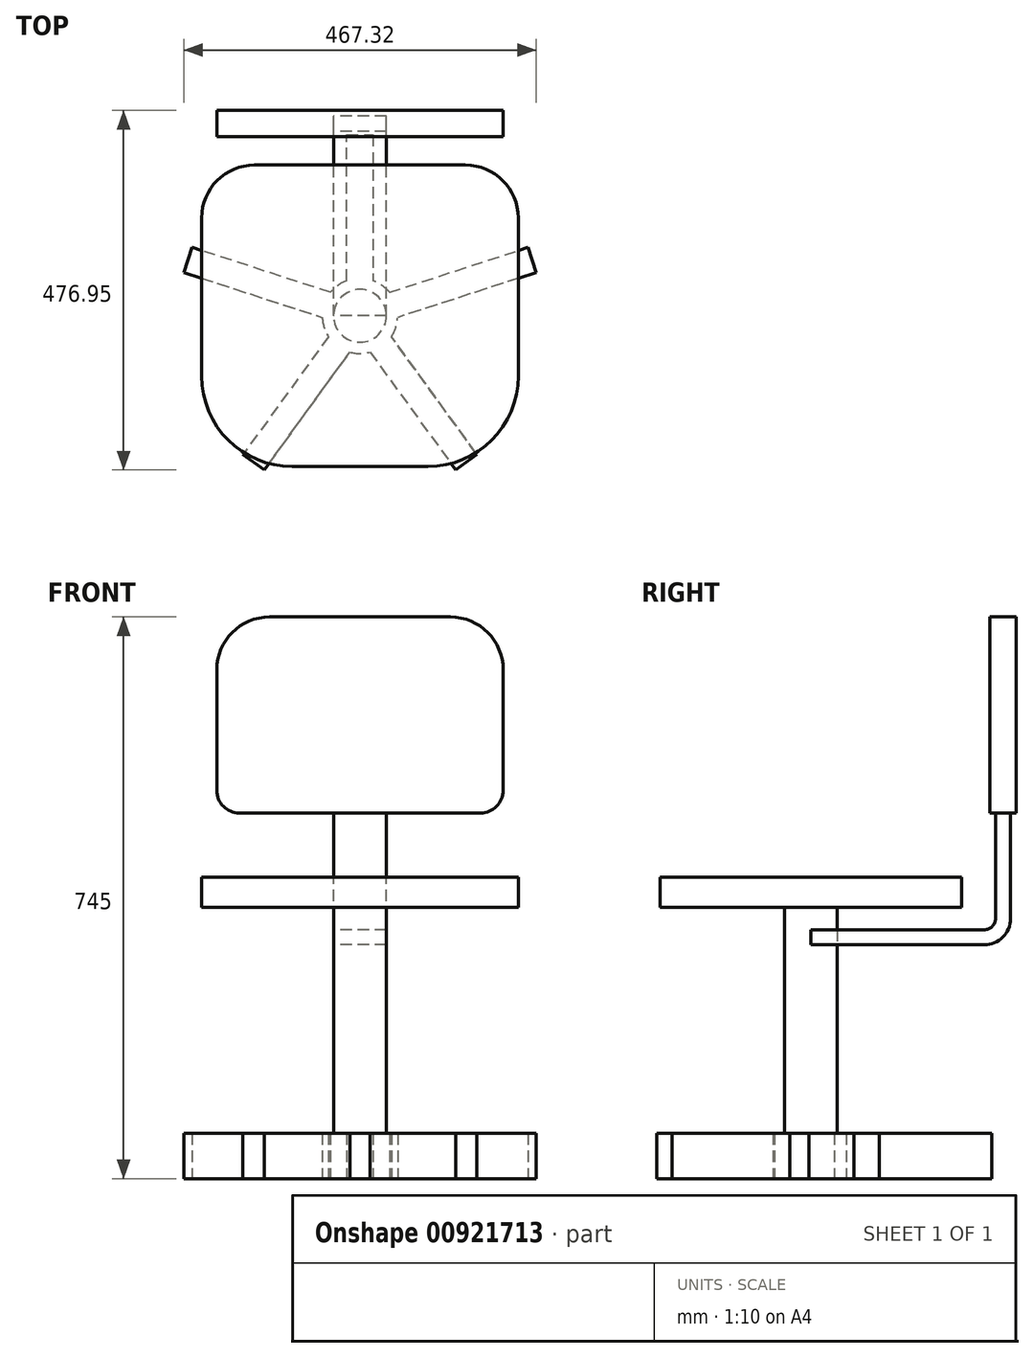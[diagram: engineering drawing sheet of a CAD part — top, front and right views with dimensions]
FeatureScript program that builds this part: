
annotation { "Feature Type Name" : "Feature", "Feature Type Description" : "" }
export const myFeature = defineFeature(function(context is Context, id is Id, definition is map)
    precondition{}
    {
        {
            var Q0;
            Q0=qCreatedBy(makeId("Top.planeOp"),FACE);
            var sketch = newSketch(context, id + "F0", { "sketchPlane" : qUnion([Q0])});
            skCircle(sketch, "E0", {"center": v(0, 0) * mm, "radius": 250 * mm, "construction": true});
            skLineSegment(sketch, "E1", {"start": v(0, 0) * mm, "end": v(0, 276.39) * mm, "construction": true});
            skLineSegment(sketch, "E2", {"start": v(0, 0) * mm, "end": v(-284.26, 92.36) * mm, "construction": true});
            skLineSegment(sketch, "E3", {"start": v(0, 0) * mm, "end": v(-174.03, -239.54) * mm, "construction": true});
            skLineSegment(sketch, "E4", {"start": v(0, 0) * mm, "end": v(174.47, -240.13) * mm, "construction": true});
            skLineSegment(sketch, "E5", {"start": v(0, 0) * mm, "end": v(285.55, 92.78) * mm, "construction": true});
            skArc(sketch, "E6", {"start": v(-49.95, -2.17) * mm, "mid": v(-47.55, -15.45) * mm, "end": v(-41.69, -27.6) * mm});
            skLineSegment(sketch, "E7", {"start": v(-39.14, 31.12) * mm, "end": v(-222.85, 90.8) * mm});
            skLineSegment(sketch, "E8", {"start": v(-222.85, 90.8) * mm, "end": v(-233.66, 57.52) * mm});
            skLineSegment(sketch, "E9", {"start": v(-233.66, 57.52) * mm, "end": v(-49.95, -2.17) * mm});
            skLineSegment(sketch, "E10", {"start": v(-41.69, -27.6) * mm, "end": v(-155.23, -183.88) * mm});
            skLineSegment(sketch, "E11", {"start": v(-155.23, -183.88) * mm, "end": v(-126.91, -204.45) * mm});
            skLineSegment(sketch, "E12", {"start": v(-126.91, -204.45) * mm, "end": v(-13.37, -48.18) * mm});
            skLineSegment(sketch, "E13", {"start": v(13.37, -48.18) * mm, "end": v(126.91, -204.45) * mm});
            skLineSegment(sketch, "E14", {"start": v(126.91, -204.45) * mm, "end": v(155.23, -183.88) * mm});
            skLineSegment(sketch, "E15", {"start": v(155.23, -183.88) * mm, "end": v(41.69, -27.6) * mm});
            skLineSegment(sketch, "E16", {"start": v(39.14, 31.12) * mm, "end": v(222.85, 90.8) * mm});
            skLineSegment(sketch, "E17", {"start": v(222.85, 90.8) * mm, "end": v(233.66, 57.52) * mm});
            skLineSegment(sketch, "E18", {"start": v(233.66, 57.52) * mm, "end": v(49.95, -2.17) * mm});
            skLineSegment(sketch, "E19", {"start": v(-17.5, 46.84) * mm, "end": v(-17.5, 240) * mm});
            skLineSegment(sketch, "E20", {"start": v(-17.5, 240) * mm, "end": v(17.5, 240) * mm});
            skLineSegment(sketch, "E21", {"start": v(17.5, 240) * mm, "end": v(17.5, 46.84) * mm});
            skArc(sketch, "E22.trimOffspring", {"start": v(-13.37, -48.18) * mm, "mid": v(0, -50) * mm, "end": v(13.37, -48.18) * mm});
            skArc(sketch, "E23.trimOffspring", {"start": v(41.69, -27.6) * mm, "mid": v(47.55, -15.45) * mm, "end": v(49.95, -2.17) * mm});
            skArc(sketch, "E24.trimOffspring", {"start": v(39.14, 31.12) * mm, "mid": v(29.39, 40.45) * mm, "end": v(17.5, 46.84) * mm});
            skArc(sketch, "E25.trimOffspring", {"start": v(-17.5, 46.84) * mm, "mid": v(-29.39, 40.45) * mm, "end": v(-39.14, 31.12) * mm});
            skSolve(sketch);
        }
        {
            var Q0;
            Q0 = qSketchRegion(id + "F0", true);
            extrude(context, id + "F1", {"entities" : qUnion([Q0]), "depth" : 60 * mm, "offsetDistance" : 25 * mm});
        }
        {
            var Q0;
            Q0=makeQuery(id+"F1.opExtrude","CAP_FACE",FACE,{"disambiguationData":[OSD([sQuery(id+"F0.wireOp",EDGE,"E6"),sQuery(id+"F0.wireOp",EDGE,"E7"),sQuery(id+"F0.wireOp",EDGE,"E8"),sQuery(id+"F0.wireOp",EDGE,"E9"),sQuery(id+"F0.wireOp",EDGE,"E10"),sQuery(id+"F0.wireOp",EDGE,"E11"),sQuery(id+"F0.wireOp",EDGE,"E12"),sQuery(id+"F0.wireOp",EDGE,"E13"),sQuery(id+"F0.wireOp",EDGE,"E14"),sQuery(id+"F0.wireOp",EDGE,"E15"),sQuery(id+"F0.wireOp",EDGE,"E16"),sQuery(id+"F0.wireOp",EDGE,"E17"),sQuery(id+"F0.wireOp",EDGE,"E18"),sQuery(id+"F0.wireOp",EDGE,"E19"),sQuery(id+"F0.wireOp",EDGE,"E20"),sQuery(id+"F0.wireOp",EDGE,"E21"),sQuery(id+"F0.wireOp",EDGE,"E22.trimOffspring"),sQuery(id+"F0.wireOp",EDGE,"E23.trimOffspring"),sQuery(id+"F0.wireOp",EDGE,"E24.trimOffspring"),sQuery(id+"F0.wireOp",EDGE,"E25.trimOffspring")])],"isStart":false});
            var sketch = newSketch(context, id + "F2", { "sketchPlane" : qUnion([Q0])});
            skCircle(sketch, "E26", {"center": v(0, 0) * mm, "radius": 35 * mm});
            skSolve(sketch);
        }
        {
            var Q0;
            Q0 = qSketchRegion(id + "F2", true);
            extrude(context, id + "F3", {"entities" : qUnion([Q0]), "operationType" : NewBodyOperationType.ADD, "depth" : 300 * mm, "offsetDistance" : 25 * mm});
        }
        {
            var Q0;
            Q0=makeQuery(id+"F3.opExtrude","CAP_FACE",FACE,{"disambiguationData":[OSD([sQuery(id+"F2.wireOp",EDGE,"E26")])],"isStart":false});
            var sketch = newSketch(context, id + "F4", { "sketchPlane" : qUnion([Q0])});
            skLineSegment(sketch, "E27.bottom", {"start": v(210, 200) * mm, "end": v(-210, 200) * mm});
            skLineSegment(sketch, "E27.top", {"start": v(210, -200) * mm, "end": v(-210, -200) * mm});
            skLineSegment(sketch, "E27.left", {"start": v(210, 200) * mm, "end": v(210, -200) * mm});
            skLineSegment(sketch, "E27.right", {"start": v(-210, 200) * mm, "end": v(-210, -200) * mm});
            skPoint(sketch, "E27.middle", {"position": v(0, 0) * mm});
            skSolve(sketch);
        }
        {
            var Q0;
            Q0 = qSketchRegion(id + "F4", true);
            extrude(context, id + "F5", {"entities" : qUnion([Q0]), "depth" : 40 * mm, "offsetDistance" : 25 * mm});
        }
        {
            var Q0;
            Q0=makeQuery(id+"F5.opExtrude","SWEPT_EDGE",EDGE,{"disambiguationData":[OSD([sQuery(id+"F4.wireOp",EDGE,"E27.top"),sQuery(id+"F4.wireOp",EDGE,"E27.left")])]});
            var Q1;
            Q1=makeQuery(id+"F5.opExtrude","SWEPT_EDGE",EDGE,{"disambiguationData":[OSD([sQuery(id+"F4.wireOp",EDGE,"E27.top"),sQuery(id+"F4.wireOp",EDGE,"E27.right")])]});
            fillet(context, id + "F6", {"entities" : qUnion([Q0, Q1]), "radius" : 120 * mm, "tangentPropagation" : true, "allowEdgeOverflow" : false});
        }
        {
            var Q0;
            Q0=makeQuery(id+"F5.opExtrude","SWEPT_EDGE",EDGE,{"disambiguationData":[OSD([sQuery(id+"F4.wireOp",EDGE,"E27.bottom"),sQuery(id+"F4.wireOp",EDGE,"E27.left")])]});
            var Q1;
            Q1=makeQuery(id+"F5.opExtrude","SWEPT_EDGE",EDGE,{"disambiguationData":[OSD([sQuery(id+"F4.wireOp",EDGE,"E27.bottom"),sQuery(id+"F4.wireOp",EDGE,"E27.right")])]});
            fillet(context, id + "F7", {"entities" : qUnion([Q0, Q1]), "radius" : 70 * mm, "tangentPropagation" : true, "allowEdgeOverflow" : false});
        }
        {
            var Q0;
            Q0=qCreatedBy(makeId("Front.planeOp"),FACE);
            var sketch = newSketch(context, id + "F8", { "sketchPlane" : qUnion([Q0])});
            skLineSegment(sketch, "E28.bottom", {"start": v(35, 330) * mm, "end": v(-35, 330) * mm});
            skLineSegment(sketch, "E28.top", {"start": v(35, 310) * mm, "end": v(-35, 310) * mm});
            skLineSegment(sketch, "E28.left", {"start": v(35, 330) * mm, "end": v(35, 310) * mm});
            skLineSegment(sketch, "E28.right", {"start": v(-35, 330) * mm, "end": v(-35, 310) * mm});
            skLineSegment(sketch, "E29", {"start": v(0, 0) * mm, "end": v(0, 138.42) * mm, "construction": true});
            skSolve(sketch);
        }
        {
            var Q0;
            Q0=qCreatedBy(makeId("Right.planeOp"),FACE);
            var sketch = newSketch(context, id + "F9", { "sketchPlane" : qUnion([Q0])});
            skLineSegment(sketch, "E30", {"start": v(0, 315) * mm, "end": v(230, 315) * mm});
            skLineSegment(sketch, "E31", {"start": v(260, 345) * mm, "end": v(260, 485) * mm});
            skPoint(sketch, "E32.visualSharp", {"position": v(260, 315) * mm});
            skArc(sketch, "E32.filletArc", {"start": v(230, 315) * mm, "mid": v(251.21, 323.79) * mm, "end": v(260, 345) * mm});
            skSolve(sketch);
        }
        {
            var Q0;
            Q0 = qSketchRegion(id + "F8", true);
            var Q1;
            Q1 = qConstructionFilter(qBodyType(qCreatedBy(id + "F9" ,EDGE), BodyType.WIRE), ConstructionObject.NO);
            sweep(context, id + "F10", {"profiles" : qUnion([Q0]), "path" : qUnion([Q1])});
        }
        {
            var Q0;
            Q0=qCreatedBy(makeId("Right.planeOp"),FACE);
            var sketch = newSketch(context, id + "F11", { "sketchPlane" : qUnion([Q0])});
            skLineSegment(sketch, "E33.bottom", {"start": v(237.5, 745) * mm, "end": v(272.5, 745) * mm});
            skLineSegment(sketch, "E33.top", {"start": v(237.5, 485) * mm, "end": v(272.5, 485) * mm});
            skLineSegment(sketch, "E33.left", {"start": v(237.5, 745) * mm, "end": v(237.5, 485) * mm});
            skLineSegment(sketch, "E33.right", {"start": v(272.5, 745) * mm, "end": v(272.5, 485) * mm});
            skSolve(sketch);
        }
        {
            var Q0;
            Q0 = qSketchRegion(id + "F11", true);
            extrude(context, id + "F12", {"entities" : qUnion([Q0]), "operationType" : NewBodyOperationType.ADD, "endBound" : BoundingType.SYMMETRIC, "depth" : 380 * mm, "offsetDistance" : 25 * mm});
        }
        {
            var Q0;
            Q0=makeQuery(id+"F12.opExtrude","CAP_EDGE",EDGE,{"disambiguationData":[OSD([sQuery(id+"F11.wireOp",EDGE,"E33.bottom")])],"isStart":false});
            var Q1;
            Q1=makeQuery(id+"F12.opExtrude","CAP_EDGE",EDGE,{"disambiguationData":[OSD([sQuery(id+"F11.wireOp",EDGE,"E33.bottom")])],"isStart":true});
            fillet(context, id + "F13", {"entities" : qUnion([Q0, Q1]), "radius" : 70 * mm, "tangentPropagation" : true, "allowEdgeOverflow" : false});
        }
        {
            var Q0;
            Q0=makeQuery(id+"F12.opExtrude","CAP_EDGE",EDGE,{"disambiguationData":[OSD([sQuery(id+"F11.wireOp",EDGE,"E33.top")])],"isStart":true});
            var Q1;
            Q1=makeQuery(id+"F12.opExtrude","CAP_EDGE",EDGE,{"disambiguationData":[OSD([sQuery(id+"F11.wireOp",EDGE,"E33.top")])],"isStart":false});
            fillet(context, id + "F14", {"entities" : qUnion([Q0, Q1]), "radius" : 30 * mm, "tangentPropagation" : true, "allowEdgeOverflow" : false});
        }
    });
